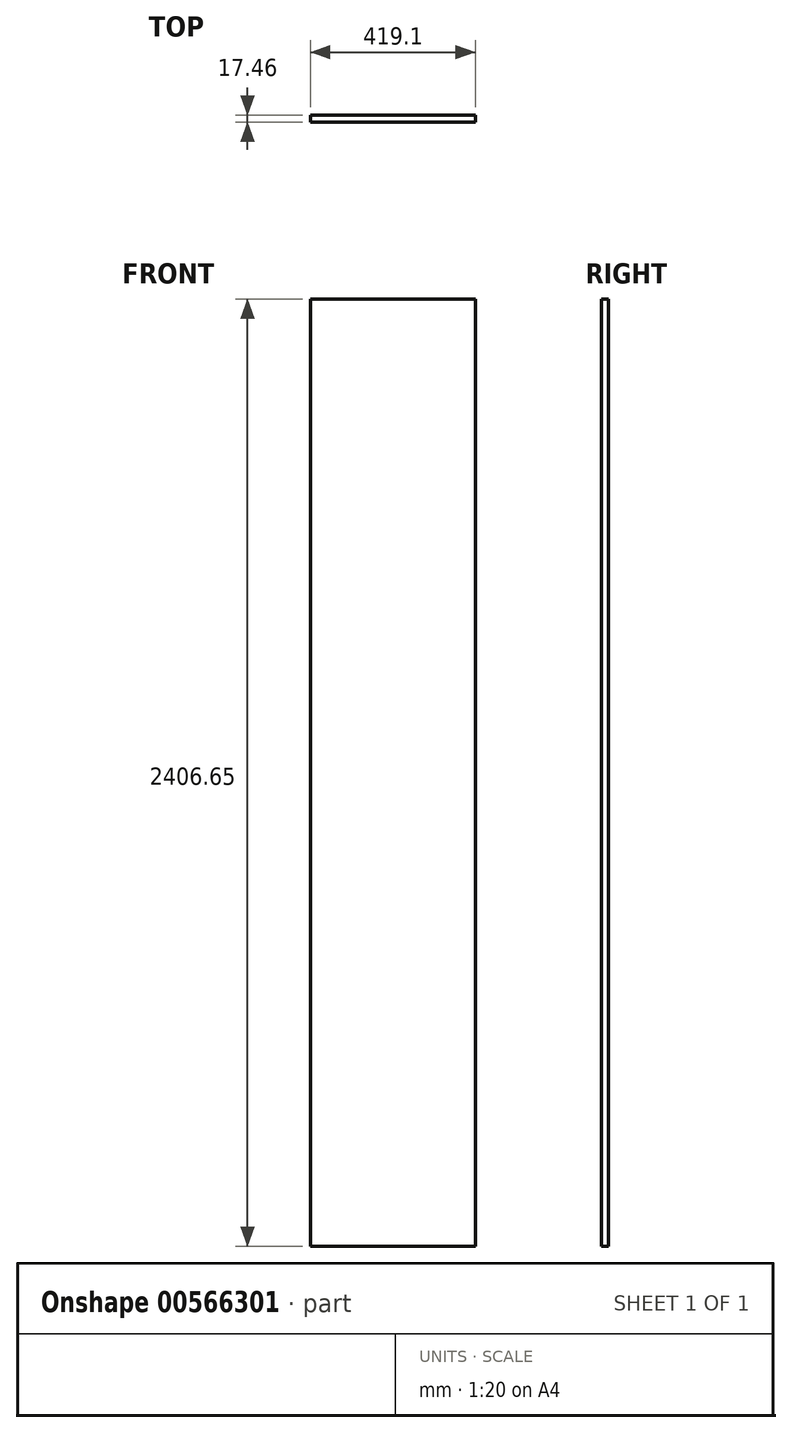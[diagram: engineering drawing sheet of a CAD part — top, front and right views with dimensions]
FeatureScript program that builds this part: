
annotation { "Feature Type Name" : "Feature", "Feature Type Description" : "" }
export const myFeature = defineFeature(function(context is Context, id is Id, definition is map)
    precondition{}
    {
        {
            var Q0;
            Q0=qCreatedBy(makeId("Front.planeOp"),FACE);
            var sketch = newSketch(context, id + "F0", { "sketchPlane" : qUnion([Q0])});
            skLineSegment(sketch, "E0.bottom", {"start": v(0, 0) * mm, "end": v(419.1, 0) * mm});
            skLineSegment(sketch, "E0.top", {"start": v(0, 2406.65) * mm, "end": v(419.1, 2406.65) * mm});
            skLineSegment(sketch, "E0.left", {"start": v(0, 0) * mm, "end": v(0, 2406.65) * mm});
            skLineSegment(sketch, "E0.right", {"start": v(419.1, 0) * mm, "end": v(419.1, 2406.65) * mm});
            skSolve(sketch);
        }
        {
            var Q0;
            Q0=makeQuery(id+"F0.imprint","IMPRINT",FACE,{"disambiguationData":[TD([[makeQuery(id+"F0.imprint","IMPRINT",EDGE,{"derivedFrom":sQuery(id+"F0.wireOp",EDGE,"E0.bottom")}),1.0]])]});
            extrude(context, id + "F1", {"entities" : qUnion([Q0]), "oppositeDirection" : true, "depth" : 17.46 * mm, "offsetDistance" : 25.4 * mm});
        }
    });
